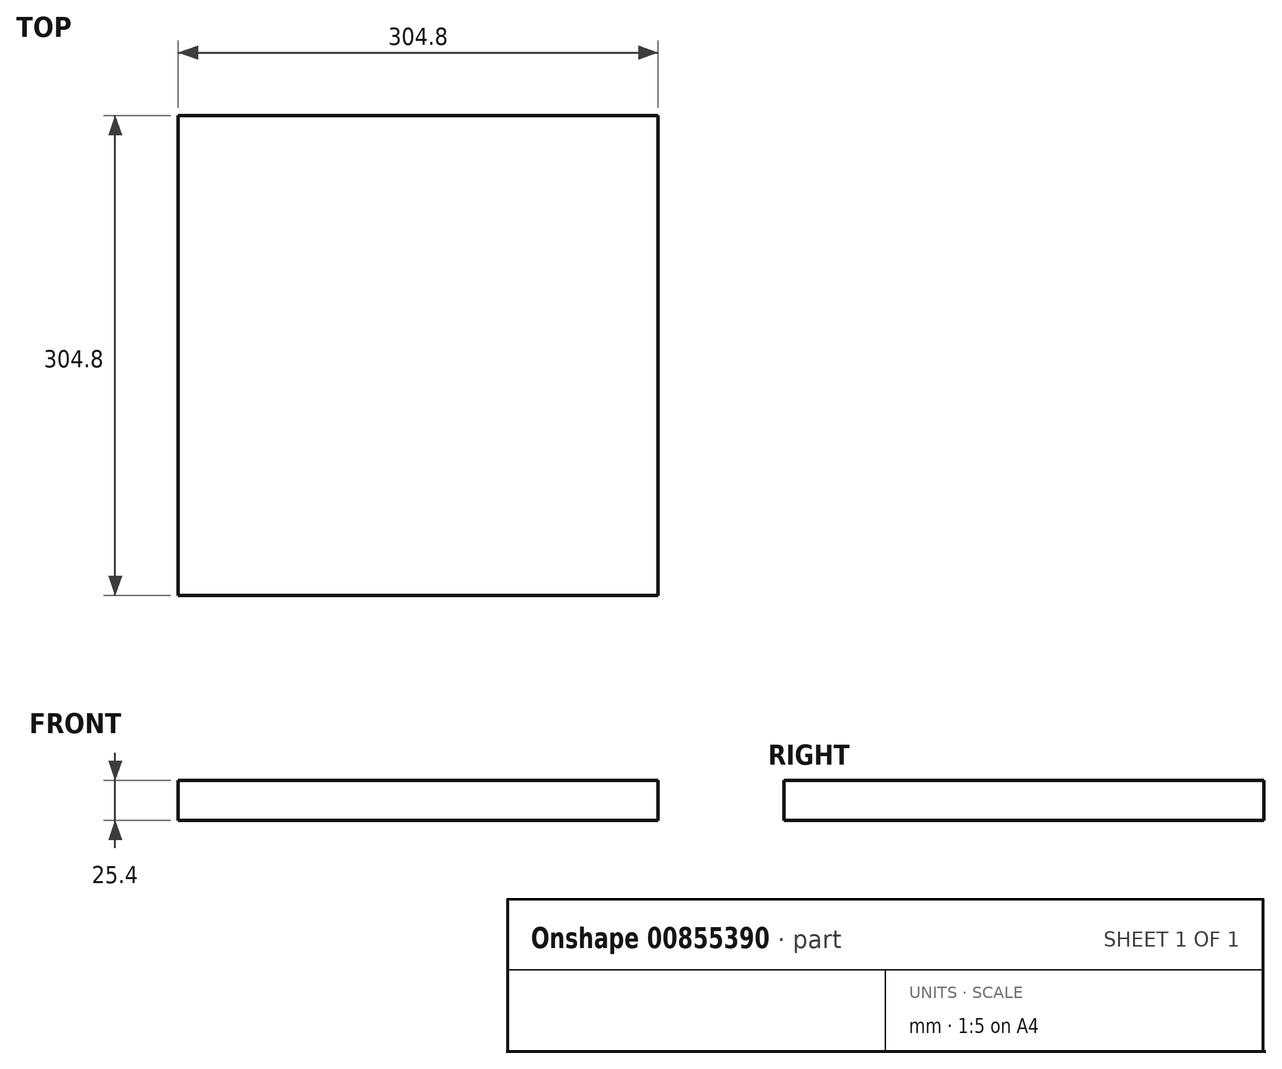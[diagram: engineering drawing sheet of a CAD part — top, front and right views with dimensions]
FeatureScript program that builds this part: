
annotation { "Feature Type Name" : "Feature", "Feature Type Description" : "" }
export const myFeature = defineFeature(function(context is Context, id is Id, definition is map)
    precondition{}
    {
        {
            var Q0;
            Q0=qCreatedBy(makeId("Top.planeOp"),FACE);
            var sketch = newSketch(context, id + "F0", { "sketchPlane" : qUnion([Q0])});
            skLineSegment(sketch, "E0.bottom", {"start": v(0, -148.82) * mm, "end": v(304.8, -148.82) * mm});
            skLineSegment(sketch, "E0.top", {"start": v(0, 155.98) * mm, "end": v(304.8, 155.98) * mm});
            skLineSegment(sketch, "E0.left", {"start": v(0, -148.82) * mm, "end": v(0, 155.98) * mm});
            skLineSegment(sketch, "E0.right", {"start": v(304.8, -148.82) * mm, "end": v(304.8, 155.98) * mm});
            skLineSegment(sketch, "E1", {"start": v(304.8, 0) * mm, "end": v(0, 0) * mm, "construction": true});
            skSolve(sketch);
        }
        {
            var Q0;
            Q0=makeQuery(id+"F0.imprint","IMPRINT",FACE,{"disambiguationData":[TD([[makeQuery(id+"F0.imprint","IMPRINT",EDGE,{"derivedFrom":sQuery(id+"F0.wireOp",EDGE,"E0.bottom")}),1.0]])]});
            extrude(context, id + "F1", {"entities" : qUnion([Q0]), "depth" : 25.4 * mm, "offsetDistance" : 25.4 * mm});
        }
    });
